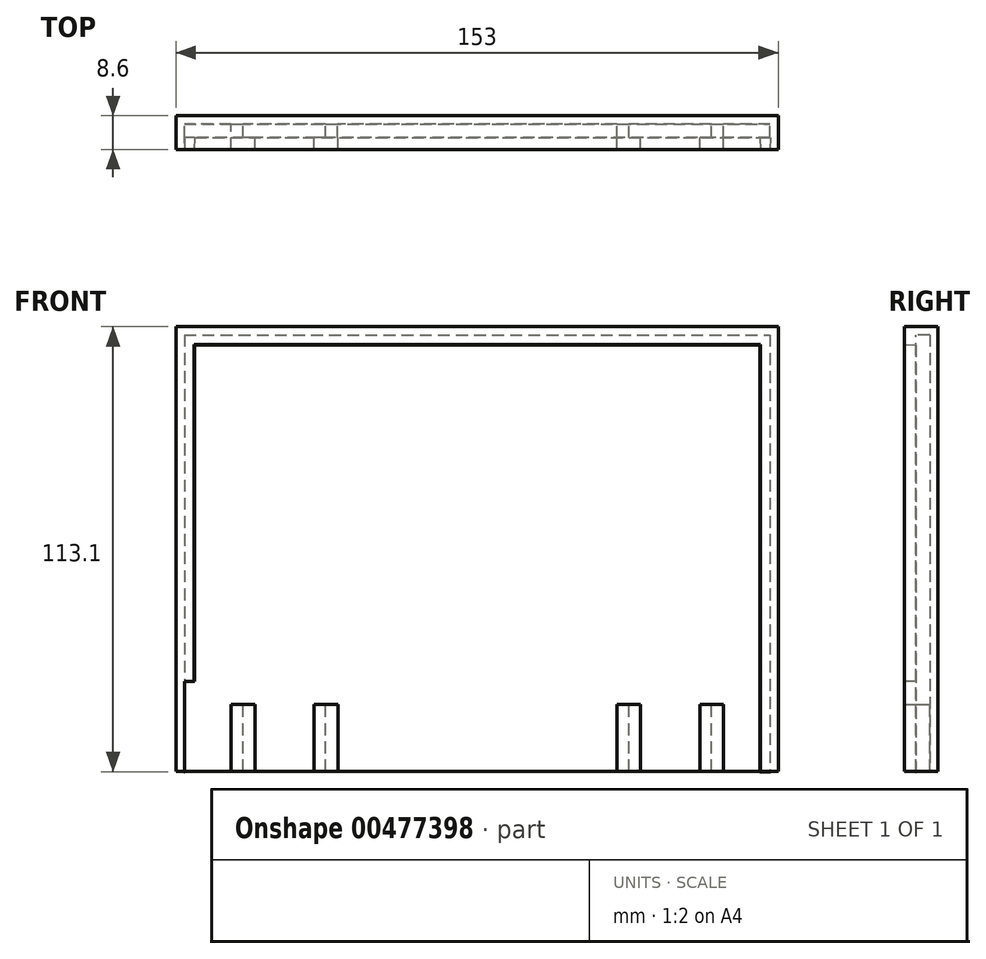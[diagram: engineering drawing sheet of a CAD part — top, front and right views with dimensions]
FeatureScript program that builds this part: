
annotation { "Feature Type Name" : "Feature", "Feature Type Description" : "" }
export const myFeature = defineFeature(function(context is Context, id is Id, definition is map)
    precondition{}
    {
        {
            var Q0;
            Q0=qCreatedBy(makeId("Front.planeOp"),FACE);
            var sketch = newSketch(context, id + "F0", { "sketchPlane" : qUnion([Q0])});
            skLineSegment(sketch, "E0.bottom", {"start": v(-85.1, 42.65) * mm, "end": v(67.9, 42.65) * mm});
            skLineSegment(sketch, "E0.top", {"start": v(-85.1, -70.35) * mm, "end": v(67.9, -70.35) * mm});
            skLineSegment(sketch, "E0.left", {"start": v(-85.1, 42.65) * mm, "end": v(-85.1, -70.35) * mm});
            skLineSegment(sketch, "E0.right", {"start": v(67.9, 42.65) * mm, "end": v(67.9, -70.35) * mm});
            skLineSegment(sketch, "E1.bottom", {"start": v(-68.1, -70.35) * mm, "end": v(-65.1, -70.35) * mm});
            skLineSegment(sketch, "E1.top", {"start": v(-68.1, -50.35) * mm, "end": v(-65.1, -50.35) * mm});
            skLineSegment(sketch, "E2", {"start": v(0, -70.35) * mm, "end": v(0, 42.65) * mm});
            skLineSegment(sketch, "E3.bottom", {"start": v(-44.1, -70.35) * mm, "end": v(-41.1, -70.35) * mm});
            skLineSegment(sketch, "E3.top", {"start": v(-44.1, -50.35) * mm, "end": v(-41.1, -50.35) * mm});
            skLineSegment(sketch, "E4.bottom", {"start": v(50.9, -70.35) * mm, "end": v(47.9, -70.35) * mm});
            skLineSegment(sketch, "E4.top", {"start": v(50.9, -50.35) * mm, "end": v(47.9, -50.35) * mm});
            skLineSegment(sketch, "E5.bottom", {"start": v(26.9, -70.35) * mm, "end": v(23.9, -70.35) * mm});
            skLineSegment(sketch, "E5.top", {"start": v(26.9, -50.35) * mm, "end": v(23.9, -50.35) * mm});
            skSolve(sketch);
        }
        {
            var Q0;
            Q0=makeQuery(id+"F0.imprint","IMPRINT",FACE,{"disambiguationData":[TD([[makeQuery(id+"F0.imprint","IMPRINT",EDGE,{"derivedFrom":sQuery(id+"F0.wireOp",EDGE,"E0.bottom")}),-1.0]])]});
            extrude(context, id + "F1", {"entities" : qUnion([Q0]), "oppositeDirection" : true, "depth" : 8.6 * mm, "offsetDistance" : 25 * mm});
        }
        {
            var Q0;
            Q0=makeQuery(id+"F1.opExtrude","CAP_FACE",FACE,{"disambiguationData":[OSD([sQuery(id+"F0.wireOp",EDGE,"E0.bottom"),sQuery(id+"F0.wireOp",EDGE,"E0.top"),sQuery(id+"F0.wireOp",EDGE,"E0.left"),sQuery(id+"F0.wireOp",EDGE,"E0.right")])],"isStart":true});
            shell(context, id + "F2", {"entities" : qUnion([Q0]), "thickness" : 2.1 * mm});
        }
        {
            var Q0;
            Q0=makeQuery(id+"F2.opShell","OFFSET_FACE",FACE,{"disambiguationData":[OSD([sQuery(id+"F0.wireOp",EDGE,"E0.top")])]});
            extrude(context, id + "F3", {"entities" : qUnion([Q0]), "operationType" : NewBodyOperationType.REMOVE, "oppositeDirection" : true, "depth" : 25 * mm, "offsetDistance" : 25 * mm});
        }
        {
            var Q0;
            Q0=makeQuery(id+"F1.opExtrude","CAP_FACE",FACE,{"disambiguationData":[OSD([sQuery(id+"F0.wireOp",EDGE,"E0.bottom"),sQuery(id+"F0.wireOp",EDGE,"E0.top"),sQuery(id+"F0.wireOp",EDGE,"E0.left"),sQuery(id+"F0.wireOp",EDGE,"E0.right")])],"isStart":true});
            var sketch = newSketch(context, id + "F4", { "sketchPlane" : qUnion([Q0])});
            skLineSegment(sketch, "E6.bottom", {"start": v(-83, -70.35) * mm, "end": v(-80.5, -70.35) * mm});
            skLineSegment(sketch, "E6.top", {"start": v(-83, 40.55) * mm, "end": v(-80.5, 40.55) * mm});
            skLineSegment(sketch, "E6.left", {"start": v(-83, -70.35) * mm, "end": v(-83, 40.55) * mm});
            skLineSegment(sketch, "E6.right", {"start": v(-80.5, -70.35) * mm, "end": v(-80.5, 40.55) * mm});
            skLineSegment(sketch, "E7.bottom", {"start": v(65.8, 40.55) * mm, "end": v(-80.5, 40.55) * mm});
            skLineSegment(sketch, "E7.top", {"start": v(65.8, 38.05) * mm, "end": v(-80.5, 38.05) * mm});
            skLineSegment(sketch, "E7.left", {"start": v(65.8, 40.55) * mm, "end": v(65.8, 38.05) * mm});
            skLineSegment(sketch, "E7.right", {"start": v(-80.5, 40.55) * mm, "end": v(-80.5, 38.05) * mm});
            skLineSegment(sketch, "E8.bottom", {"start": v(65.8, -70.35) * mm, "end": v(63.3, -70.35) * mm});
            skLineSegment(sketch, "E8.top", {"start": v(65.8, 38.05) * mm, "end": v(63.3, 38.05) * mm});
            skLineSegment(sketch, "E8.left", {"start": v(65.8, -70.35) * mm, "end": v(65.8, 38.05) * mm});
            skLineSegment(sketch, "E8.right", {"start": v(63.3, -70.35) * mm, "end": v(63.3, 38.05) * mm});
            skSolve(sketch);
        }
        {
            var Q0;
            Q0=makeQuery(id+"F4.imprint","IMPRINT",FACE,{"disambiguationData":[TD([[makeQuery(id+"F4.imprint","IMPRINT",EDGE,{"derivedFrom":sQuery(id+"F4.wireOp",EDGE,"E7.bottom")}),-1.0]])]});
            var Q1;
            Q1=makeQuery(id+"F4.imprint","IMPRINT",FACE,{"disambiguationData":[TD([[makeQuery(id+"F4.imprint","IMPRINT",EDGE,{"derivedFrom":sQuery(id+"F4.wireOp",EDGE,"E6.bottom")}),1.0]])]});
            var Q2;
            Q2=makeQuery(id+"F4.imprint","IMPRINT",FACE,{"disambiguationData":[TD([[makeQuery(id+"F4.imprint","IMPRINT",EDGE,{"derivedFrom":sQuery(id+"F4.wireOp",EDGE,"E8.bottom")}),-1.0]])]});
            extrude(context, id + "F5", {"entities" : qUnion([Q0, Q1, Q2]), "operationType" : NewBodyOperationType.ADD, "oppositeDirection" : true, "depth" : 3 * mm, "offsetDistance" : 25 * mm, "hasDraft" : true, "draftAngle" : 2 * degree});
        }
        {
            var Q0;
            {var subQ0=sQuery(id+"F0.wireOp",EDGE,"E5.bottom");var subQ1=sQuery(id+"F0.wireOp",EDGE,"E4.bottom");var subQ2=sQuery(id+"F0.wireOp",EDGE,"E3.bottom");var subQ3=sQuery(id+"F0.wireOp",EDGE,"E1.bottom");var subQ4=sQuery(id+"F0.wireOp",EDGE,"E0.top");Q0=makeQuery(id+"F3.boolean.opBoolean","MERGE",FACE,{"derivedFrom":[makeQuery(id+"F2.opShell","OFFSET_FACE",FACE,{"disambiguationData":[OSD([sQuery(id+"F0.wireOp",EDGE,"E0.bottom"),subQ4,sQuery(id+"F0.wireOp",EDGE,"E0.left"),sQuery(id+"F0.wireOp",EDGE,"E0.right"),subQ3,subQ2,subQ1,subQ0])]}),makeQuery(id+"F3.opExtrude","SWEPT_FACE",FACE,{"disambiguationData":[OSD([subQ4,subQ3,subQ2,subQ1,subQ0]),TDD([makeQuery(id+"F2.opShell","OFFSET_EDGE",EDGE,{"disambiguationData":[OSD([subQ4,subQ3,subQ2,subQ1,subQ0]),TDD([makeQuery(id+"F1.opExtrude","CAP_EDGE",EDGE,{"disambiguationData":[OSD([subQ4,subQ3,subQ2,subQ1,subQ0])],"isStart":false})])]})])]})]});}
            var sketch = newSketch(context, id + "F6", { "sketchPlane" : qUnion([Q0])});
            skLineSegment(sketch, "E9.bottom", {"start": v(-71.1, -70.35) * mm, "end": v(-68.1, -70.35) * mm});
            skLineSegment(sketch, "E9.top", {"start": v(-71.1, -53.35) * mm, "end": v(-68.1, -53.35) * mm});
            skLineSegment(sketch, "E9.left", {"start": v(-71.1, -70.35) * mm, "end": v(-71.1, -53.35) * mm});
            skLineSegment(sketch, "E9.right", {"start": v(-68.1, -70.35) * mm, "end": v(-68.1, -53.35) * mm});
            skLineSegment(sketch, "E10.bottom", {"start": v(-47.1, -70.35) * mm, "end": v(-44.1, -70.35) * mm});
            skLineSegment(sketch, "E10.top", {"start": v(-47.1, -53.35) * mm, "end": v(-44.1, -53.35) * mm});
            skLineSegment(sketch, "E10.left", {"start": v(-47.1, -70.35) * mm, "end": v(-47.1, -53.35) * mm});
            skLineSegment(sketch, "E10.right", {"start": v(-44.1, -70.35) * mm, "end": v(-44.1, -53.35) * mm});
            skLineSegment(sketch, "E11.bottom", {"start": v(26.9, -70.35) * mm, "end": v(29.9, -70.35) * mm});
            skLineSegment(sketch, "E11.top", {"start": v(26.9, -53.35) * mm, "end": v(29.9, -53.35) * mm});
            skLineSegment(sketch, "E11.left", {"start": v(26.9, -70.35) * mm, "end": v(26.9, -53.35) * mm});
            skLineSegment(sketch, "E11.right", {"start": v(29.9, -70.35) * mm, "end": v(29.9, -53.35) * mm});
            skLineSegment(sketch, "E12.bottom", {"start": v(50.9, -70.35) * mm, "end": v(53.9, -70.35) * mm});
            skLineSegment(sketch, "E12.top", {"start": v(50.9, -53.35) * mm, "end": v(53.9, -53.35) * mm});
            skLineSegment(sketch, "E12.left", {"start": v(50.9, -70.35) * mm, "end": v(50.9, -53.35) * mm});
            skLineSegment(sketch, "E12.right", {"start": v(53.9, -70.35) * mm, "end": v(53.9, -53.35) * mm});
            skSolve(sketch);
        }
        {
            var Q0;
            Q0=makeQuery(id+"F6.imprint","IMPRINT",FACE,{"disambiguationData":[TD([[makeQuery(id+"F6.imprint","IMPRINT",EDGE,{"derivedFrom":sQuery(id+"F6.wireOp",EDGE,"E9.bottom")}),-1.0]])]});
            var Q1;
            Q1=makeQuery(id+"F6.imprint","IMPRINT",FACE,{"disambiguationData":[TD([[makeQuery(id+"F6.imprint","IMPRINT",EDGE,{"derivedFrom":sQuery(id+"F6.wireOp",EDGE,"E10.bottom")}),-1.0]])]});
            var Q2;
            Q2=makeQuery(id+"F6.imprint","IMPRINT",FACE,{"disambiguationData":[TD([[makeQuery(id+"F6.imprint","IMPRINT",EDGE,{"derivedFrom":sQuery(id+"F6.wireOp",EDGE,"E11.bottom")}),-1.0]])]});
            var Q3;
            Q3=makeQuery(id+"F6.imprint","IMPRINT",FACE,{"disambiguationData":[TD([[makeQuery(id+"F6.imprint","IMPRINT",EDGE,{"derivedFrom":sQuery(id+"F6.wireOp",EDGE,"E12.bottom")}),-1.0]])]});
            extrude(context, id + "F7", {"entities" : qUnion([Q0, Q1, Q2, Q3]), "operationType" : NewBodyOperationType.ADD, "depth" : 3.5 * mm, "offsetDistance" : 25 * mm});
        }
        {
            var Q0;
            Q0=makeQuery(id+"F7.opExtrude","CAP_FACE",FACE,{"disambiguationData":[OSD([sQuery(id+"F6.wireOp",EDGE,"E9.bottom"),sQuery(id+"F6.wireOp",EDGE,"E9.top"),sQuery(id+"F6.wireOp",EDGE,"E9.left"),sQuery(id+"F6.wireOp",EDGE,"E9.right")])],"isStart":false});
            var sketch = newSketch(context, id + "F8", { "sketchPlane" : qUnion([Q0])});
            skLineSegment(sketch, "E13.bottom", {"start": v(-71.1, -53.35) * mm, "end": v(-65.1, -53.35) * mm});
            skLineSegment(sketch, "E13.top", {"start": v(-71.1, -70.35) * mm, "end": v(-65.1, -70.35) * mm});
            skLineSegment(sketch, "E13.left", {"start": v(-71.1, -53.35) * mm, "end": v(-71.1, -70.35) * mm});
            skLineSegment(sketch, "E13.right", {"start": v(-65.1, -53.35) * mm, "end": v(-65.1, -70.35) * mm});
            skLineSegment(sketch, "E14.bottom", {"start": v(-44, -53.35) * mm, "end": v(-50, -53.35) * mm});
            skLineSegment(sketch, "E14.top", {"start": v(-44, -70.35) * mm, "end": v(-50, -70.35) * mm});
            skLineSegment(sketch, "E14.left", {"start": v(-44, -53.35) * mm, "end": v(-44, -70.35) * mm});
            skLineSegment(sketch, "E14.right", {"start": v(-50, -53.35) * mm, "end": v(-50, -70.35) * mm});
            skPoint(sketch, "E15.oppositeSnap0", {"position": v(-47, -70.35) * mm});
            skLineSegment(sketch, "E15.bottom", {"start": v(26.91, -53.35) * mm, "end": v(32.91, -53.35) * mm});
            skLineSegment(sketch, "E15.top", {"start": v(26.91, -70.35) * mm, "end": v(32.91, -70.35) * mm});
            skLineSegment(sketch, "E15.left", {"start": v(26.91, -53.35) * mm, "end": v(26.91, -70.35) * mm});
            skLineSegment(sketch, "E15.right", {"start": v(32.91, -53.35) * mm, "end": v(32.91, -70.35) * mm});
            skLineSegment(sketch, "E16.bottom", {"start": v(53.94, -53.35) * mm, "end": v(47.94, -53.35) * mm});
            skLineSegment(sketch, "E16.top", {"start": v(53.94, -70.35) * mm, "end": v(47.94, -70.35) * mm});
            skLineSegment(sketch, "E16.left", {"start": v(53.94, -53.35) * mm, "end": v(53.94, -70.35) * mm});
            skLineSegment(sketch, "E16.right", {"start": v(47.94, -53.35) * mm, "end": v(47.94, -70.35) * mm});
            skSolve(sketch);
        }
        {
            var Q0;
            Q0 = qSketchRegion(id + "F8", true);
            extrude(context, id + "F9", {"entities" : qUnion([Q0]), "operationType" : NewBodyOperationType.ADD, "depth" : 3 * mm, "offsetDistance" : 25 * mm});
        }
        {
            var Q0;
            Q0=makeQuery(id+"F4.imprint","IMPRINT",FACE,{"disambiguationData":[TD([[makeQuery(id+"F4.imprint","IMPRINT",EDGE,{"derivedFrom":sQuery(id+"F4.wireOp",EDGE,"E6.bottom")}),1.0]])]});
            var sketch = newSketch(context, id + "F10", { "sketchPlane" : qUnion([Q0])});
            skLineSegment(sketch, "E17.bottom", {"start": v(-78.06, -73.11) * mm, "end": v(-82.97, -73.11) * mm});
            skLineSegment(sketch, "E17.top", {"start": v(-78.06, -47.45) * mm, "end": v(-82.97, -47.45) * mm});
            skLineSegment(sketch, "E17.left", {"start": v(-78.06, -73.11) * mm, "end": v(-78.06, -47.45) * mm});
            skLineSegment(sketch, "E17.right", {"start": v(-82.97, -73.11) * mm, "end": v(-82.97, -47.45) * mm});
            skSolve(sketch);
        }
        {
            var Q0;
            {var subQ0=sQuery(id+"F10.wireOp",EDGE,"E17.right");var subQ1=sQuery(id+"F10.wireOp",EDGE,"E17.top");var subQ2=makeQuery(id+"F10.imprint","INTERSECT",VERTEX,{"derivedFrom":[subQ1,subQ0]});Q0=makeQuery(id+"F10.imprint","IMPRINT",FACE,{"disambiguationData":[TD([[makeQuery(id+"F10.imprint","IMPRINT",EDGE,{"disambiguationData":[TD([[subQ2,1.0]])],"derivedFrom":subQ1}),1.0]])]});}
            var Q1;
            {var subQ1=sQuery(id+"F10.wireOp",EDGE,"E17.bottom");Q1=makeQuery(id+"F10.imprint","IMPRINT",FACE,{"disambiguationData":[TD([[makeQuery(id+"F10.imprint","IMPRINT",EDGE,{"derivedFrom":subQ1}),-1.0]])]});}
            extrude(context, id + "F11", {"entities" : qUnion([Q0, Q1]), "operationType" : NewBodyOperationType.REMOVE, "oppositeDirection" : true, "depth" : 4 * mm, "offsetDistance" : 25 * mm});
        }
    });
